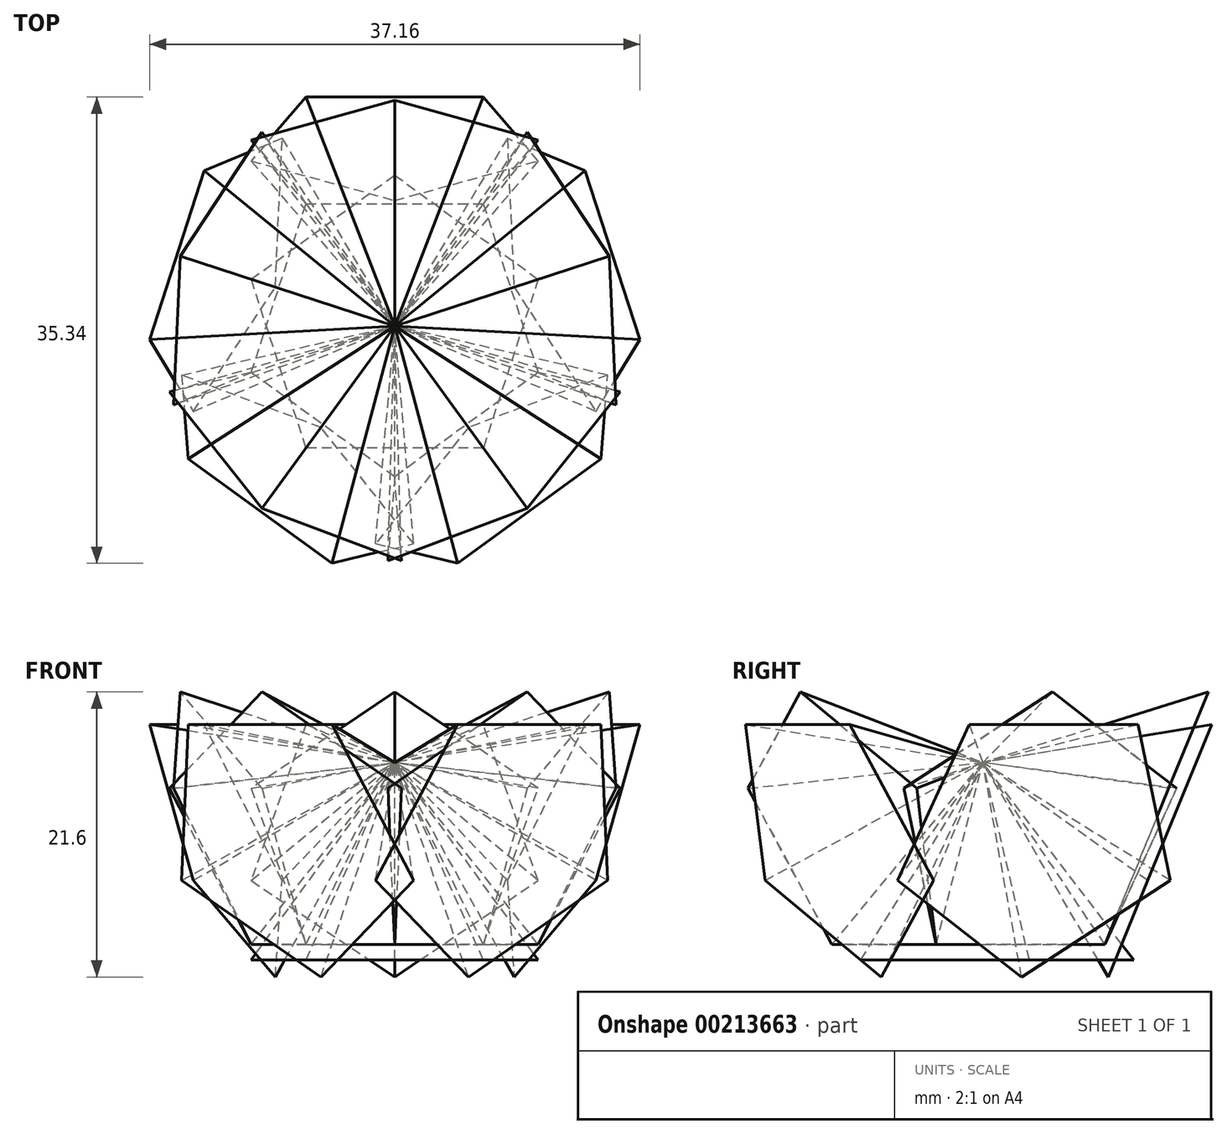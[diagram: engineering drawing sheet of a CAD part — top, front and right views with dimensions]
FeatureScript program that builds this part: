
annotation { "Feature Type Name" : "Feature", "Feature Type Description" : "" }
export const myFeature = defineFeature(function(context is Context, id is Id, definition is map)
    precondition{}
    {
        {
            assignVariable(context, id + "F0", {"name" : "a", "anyValue" : 0.9});
        }
        {
            var Q0;
            Q0=qCreatedBy(makeId("Top.planeOp"),FACE);
            cPlane(context, id + "F1", {"entities" : qUnion([Q0]), "cplaneType" : CPlaneType.OFFSET, "offset" : getVariable(context, 'a') * (1 + sin(18 * degree)) * mm, "width" : 152.4 * mm, "height" : 152.4 * mm});
        }
        {
            var Q0;
            Q0=qCreatedBy(makeId("Top.planeOp"),FACE);
            var sketch = newSketch(context, id + "F2", { "sketchPlane" : qUnion([Q0])});
            skCircle(sketch, "E0.cCircle", {"center": v(0, 0) * mm, "radius": 11.43 * mm, "construction": true});
            skLineSegment(sketch, "E0.0", {"start": v(10.87, 3.53) * mm, "end": v(6.72, -9.25) * mm});
            skLineSegment(sketch, "E0.1", {"start": v(6.72, -9.25) * mm, "end": v(-6.72, -9.25) * mm});
            skLineSegment(sketch, "E0.2", {"start": v(-6.72, -9.25) * mm, "end": v(-10.87, 3.53) * mm});
            skLineSegment(sketch, "E0.3", {"start": v(-10.87, 3.53) * mm, "end": v(0, 11.43) * mm});
            skLineSegment(sketch, "E0.4", {"start": v(0, 11.43) * mm, "end": v(10.87, 3.53) * mm});
            skSolve(sketch);
        }
        {
            var Q0;
            Q0=qCreatedBy(id+"F1.planeOp",FACE);
            var sketch = newSketch(context, id + "F3", { "sketchPlane" : qUnion([Q0])});
            skCircle(sketch, "E1.cCircle", {"center": v(0, 0) * mm, "radius": 11.43 * mm, "construction": true});
            skLineSegment(sketch, "E1.0", {"start": v(6.72, 9.25) * mm, "end": v(10.87, -3.53) * mm});
            skLineSegment(sketch, "E1.1", {"start": v(10.87, -3.53) * mm, "end": v(0, -11.43) * mm});
            skLineSegment(sketch, "E1.2", {"start": v(0, -11.43) * mm, "end": v(-10.87, -3.53) * mm});
            skLineSegment(sketch, "E1.3", {"start": v(-10.87, -3.53) * mm, "end": v(-6.72, 9.25) * mm});
            skLineSegment(sketch, "E1.4", {"start": v(-6.72, 9.25) * mm, "end": v(6.72, 9.25) * mm});
            skSolve(sketch);
        }
        {
            var Q0;
            Q0=qCreatedBy(makeId("Front.planeOp"),FACE);
            var sketch = newSketch(context, id + "F4", { "sketchPlane" : qUnion([Q0])});
            skLineSegment(sketch, "E2", {"start": v(0, 0) * mm, "end": v(0, 29.92) * mm});
            skPoint(sketch, "E3", {"position": v(0, 14.96) * mm});
            skSolve(sketch);
        }
        {
            var Q0;
            Q0=makeQuery(id+"F2.imprint","IMPRINT",FACE,{"disambiguationData":[TD([[makeQuery(id+"F2.imprint","IMPRINT",EDGE,{"derivedFrom":sQuery(id+"F2.wireOp",EDGE,"E0.0")}),-1.0]])]});
            var Q1;
            Q1=sQuery(id+"F4.wireOp",VERTEX,"E3");
            loft(context, id + "F5", {"sheetProfilesArray" : [{ "sheetProfileEntities" : qUnion([Q0]) }, { "sheetProfileEntities" : qUnion([Q1]) }]});
        }
        {
            var Q0;
            Q0=makeQuery(id+"F3.imprint","IMPRINT",FACE,{"disambiguationData":[TD([[makeQuery(id+"F3.imprint","IMPRINT",EDGE,{"derivedFrom":sQuery(id+"F3.wireOp",EDGE,"E1.0")}),-1.0]])]});
            var Q1;
            Q1=sQuery(id+"F4.wireOp",VERTEX,"E3");
            loft(context, id + "F6", {"sheetProfilesArray" : [{ "sheetProfileEntities" : qUnion([Q0]) }, { "sheetProfileEntities" : qUnion([Q1]) }]});
        }
        {
            var Q0;
            Q0=makeQuery(id+"F6.opLoft","SWEPT_BODY",BODY,{"disambiguationData":[OSD([makeQuery(id+"F3.imprint","IMPRINT",FACE,{"disambiguationData":[TD([[makeQuery(id+"F3.imprint","IMPRINT",EDGE,{"derivedFrom":sQuery(id+"F3.wireOp",EDGE,"E1.0")}),-1.0]])]}),sQuery(id+"F4.wireOp",VERTEX,"E3")])]});
            var Q1;
            Q1=makeQuery(id+"F5.opLoft","SWEPT_BODY",BODY,{"disambiguationData":[OSD([makeQuery(id+"F2.imprint","IMPRINT",FACE,{"disambiguationData":[TD([[makeQuery(id+"F2.imprint","IMPRINT",EDGE,{"derivedFrom":sQuery(id+"F2.wireOp",EDGE,"E0.0")}),-1.0]])]}),sQuery(id+"F4.wireOp",VERTEX,"E3")])]});
            var Q2;
            Q2=makeQuery(id+"F6.opLoft","SWEPT_FACE",FACE,{"disambiguationData":[OSD([sQuery(id+"F3.wireOp",EDGE,"E1.0"),sQuery(id+"F3.wireOp",EDGE,"E1.1"),sQuery(id+"F3.wireOp",EDGE,"E1.4")])]});
            mirror(context, id + "F7", {"entities" : qUnion([Q0, Q1]), "mirrorPlane" : qUnion([Q2])});
        }
        {
            var Q0;
            Q0=makeQuery(id+"F6.opLoft","SWEPT_BODY",BODY,{"disambiguationData":[OSD([makeQuery(id+"F3.imprint","IMPRINT",FACE,{"disambiguationData":[TD([[makeQuery(id+"F3.imprint","IMPRINT",EDGE,{"derivedFrom":sQuery(id+"F3.wireOp",EDGE,"E1.0")}),-1.0]])]}),sQuery(id+"F4.wireOp",VERTEX,"E3")])]});
            var Q1;
            Q1=makeQuery(id+"F5.opLoft","SWEPT_BODY",BODY,{"disambiguationData":[OSD([makeQuery(id+"F2.imprint","IMPRINT",FACE,{"disambiguationData":[TD([[makeQuery(id+"F2.imprint","IMPRINT",EDGE,{"derivedFrom":sQuery(id+"F2.wireOp",EDGE,"E0.0")}),-1.0]])]}),sQuery(id+"F4.wireOp",VERTEX,"E3")])]});
            var Q2;
            Q2=makeQuery(id+"F6.opLoft","SWEPT_FACE",FACE,{"disambiguationData":[OSD([sQuery(id+"F3.wireOp",EDGE,"E1.1"),sQuery(id+"F3.wireOp",EDGE,"E1.2"),sQuery(id+"F3.wireOp",EDGE,"E1.3")])]});
            mirror(context, id + "F8", {"entities" : qUnion([Q0, Q1]), "mirrorPlane" : qUnion([Q2])});
        }
        {
            var Q0;
            Q0=makeQuery(id+"F6.opLoft","SWEPT_BODY",BODY,{"disambiguationData":[OSD([makeQuery(id+"F3.imprint","IMPRINT",FACE,{"disambiguationData":[TD([[makeQuery(id+"F3.imprint","IMPRINT",EDGE,{"derivedFrom":sQuery(id+"F3.wireOp",EDGE,"E1.0")}),-1.0]])]}),sQuery(id+"F4.wireOp",VERTEX,"E3")])]});
            var Q1;
            Q1=makeQuery(id+"F5.opLoft","SWEPT_BODY",BODY,{"disambiguationData":[OSD([makeQuery(id+"F2.imprint","IMPRINT",FACE,{"disambiguationData":[TD([[makeQuery(id+"F2.imprint","IMPRINT",EDGE,{"derivedFrom":sQuery(id+"F2.wireOp",EDGE,"E0.0")}),-1.0]])]}),sQuery(id+"F4.wireOp",VERTEX,"E3")])]});
            var Q2;
            Q2=makeQuery(id+"F6.opLoft","SWEPT_FACE",FACE,{"disambiguationData":[OSD([sQuery(id+"F3.wireOp",EDGE,"E1.0"),sQuery(id+"F3.wireOp",EDGE,"E1.1"),sQuery(id+"F3.wireOp",EDGE,"E1.2")])]});
            mirror(context, id + "F9", {"entities" : qUnion([Q0, Q1]), "mirrorPlane" : qUnion([Q2])});
        }
        {
            var Q0;
            Q0=makeQuery(id+"F6.opLoft","SWEPT_BODY",BODY,{"disambiguationData":[OSD([makeQuery(id+"F3.imprint","IMPRINT",FACE,{"disambiguationData":[TD([[makeQuery(id+"F3.imprint","IMPRINT",EDGE,{"derivedFrom":sQuery(id+"F3.wireOp",EDGE,"E1.0")}),-1.0]])]}),sQuery(id+"F4.wireOp",VERTEX,"E3")])]});
            var Q1;
            Q1=makeQuery(id+"F5.opLoft","SWEPT_BODY",BODY,{"disambiguationData":[OSD([makeQuery(id+"F2.imprint","IMPRINT",FACE,{"disambiguationData":[TD([[makeQuery(id+"F2.imprint","IMPRINT",EDGE,{"derivedFrom":sQuery(id+"F2.wireOp",EDGE,"E0.0")}),-1.0]])]}),sQuery(id+"F4.wireOp",VERTEX,"E3")])]});
            var Q2;
            Q2=makeQuery(id+"F6.opLoft","SWEPT_FACE",FACE,{"disambiguationData":[OSD([sQuery(id+"F3.wireOp",EDGE,"E1.0"),sQuery(id+"F3.wireOp",EDGE,"E1.3"),sQuery(id+"F3.wireOp",EDGE,"E1.4")])]});
            mirror(context, id + "F10", {"entities" : qUnion([Q0, Q1]), "mirrorPlane" : qUnion([Q2])});
        }
        {
            var Q0;
            Q0=makeQuery(id+"F6.opLoft","SWEPT_BODY",BODY,{"disambiguationData":[OSD([makeQuery(id+"F3.imprint","IMPRINT",FACE,{"disambiguationData":[TD([[makeQuery(id+"F3.imprint","IMPRINT",EDGE,{"derivedFrom":sQuery(id+"F3.wireOp",EDGE,"E1.0")}),-1.0]])]}),sQuery(id+"F4.wireOp",VERTEX,"E3")])]});
            var Q1;
            Q1=makeQuery(id+"F5.opLoft","SWEPT_BODY",BODY,{"disambiguationData":[OSD([makeQuery(id+"F2.imprint","IMPRINT",FACE,{"disambiguationData":[TD([[makeQuery(id+"F2.imprint","IMPRINT",EDGE,{"derivedFrom":sQuery(id+"F2.wireOp",EDGE,"E0.0")}),-1.0]])]}),sQuery(id+"F4.wireOp",VERTEX,"E3")])]});
            var Q2;
            Q2=makeQuery(id+"F6.opLoft","SWEPT_FACE",FACE,{"disambiguationData":[OSD([sQuery(id+"F3.wireOp",EDGE,"E1.2"),sQuery(id+"F3.wireOp",EDGE,"E1.3"),sQuery(id+"F3.wireOp",EDGE,"E1.4")])]});
            mirror(context, id + "F11", {"entities" : qUnion([Q0, Q1]), "mirrorPlane" : qUnion([Q2])});
        }
    });
